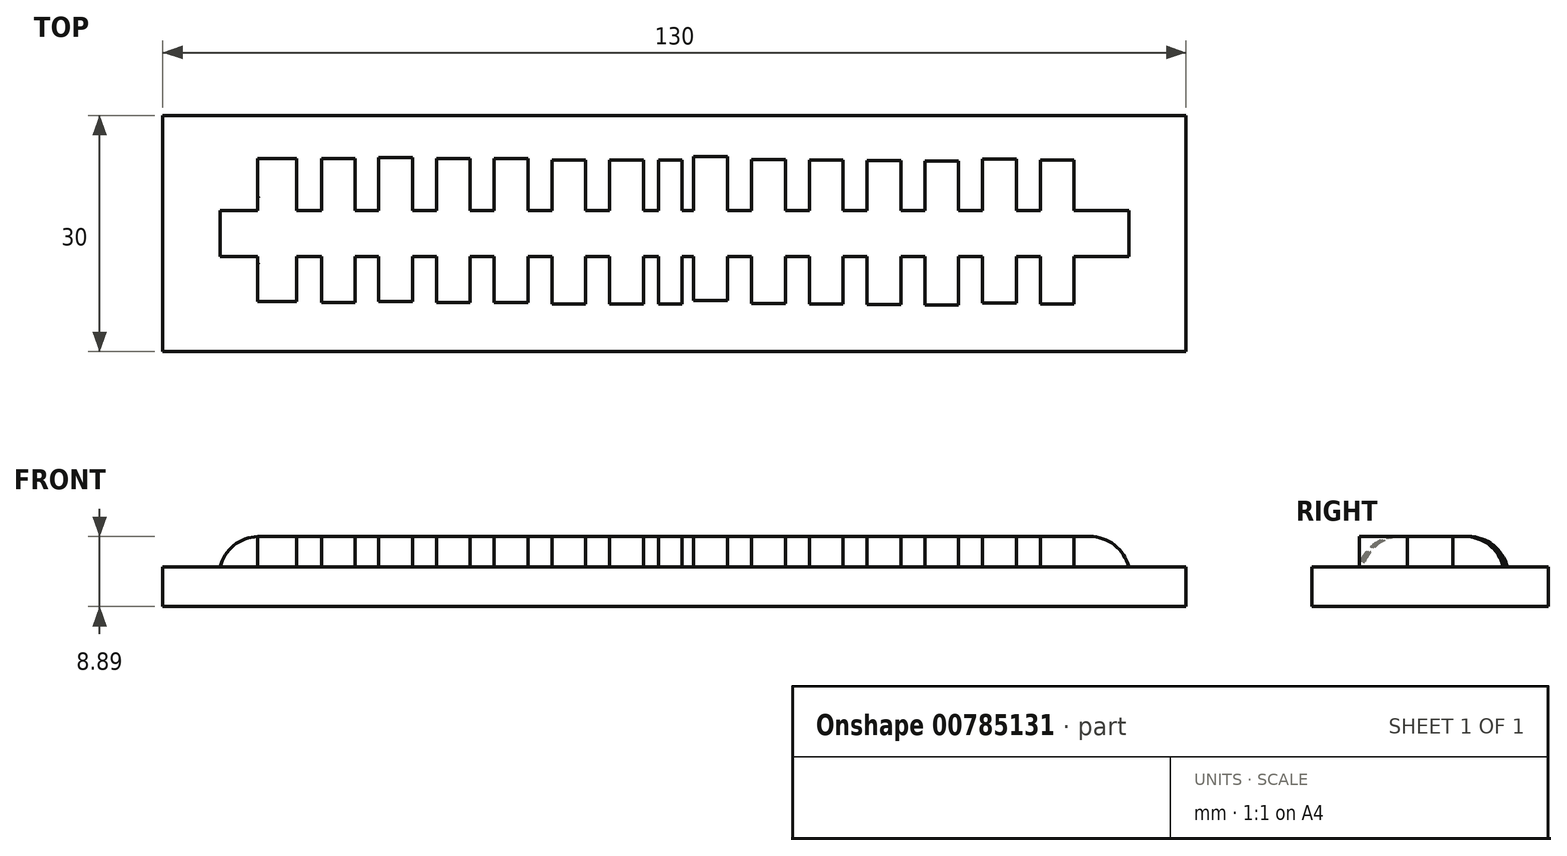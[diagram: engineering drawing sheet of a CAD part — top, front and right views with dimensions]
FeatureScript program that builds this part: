
annotation { "Feature Type Name" : "Feature", "Feature Type Description" : "" }
export const myFeature = defineFeature(function(context is Context, id is Id, definition is map)
    precondition{}
    {
        {
            var Q0;
            Q0=qCreatedBy(makeId("Top.planeOp"),FACE);
            var sketch = newSketch(context, id + "F0", { "sketchPlane" : qUnion([Q0])});
            skLineSegment(sketch, "E0.bottom", {"start": v(-65, 15) * mm, "end": v(65, 15) * mm});
            skLineSegment(sketch, "E0.top", {"start": v(-65, -15) * mm, "end": v(65, -15) * mm});
            skLineSegment(sketch, "E0.left", {"start": v(-65, 15) * mm, "end": v(-65, -15) * mm});
            skLineSegment(sketch, "E0.right", {"start": v(65, 15) * mm, "end": v(65, -15) * mm});
            skPoint(sketch, "E0.middle", {"position": v(0, 0) * mm});
            skSolve(sketch);
        }
        {
            var Q0;
            Q0 = qSketchRegion(id + "F0", true);
            extrude(context, id + "F1", {"entities" : qUnion([Q0]), "depth" : 5 * mm, "offsetDistance" : 25.4 * mm});
        }
        {
            var Q0;
            Q0=qCreatedBy(makeId("Top.planeOp"),FACE);
            var sketch = newSketch(context, id + "F2", { "sketchPlane" : qUnion([Q0])});
            skLineSegment(sketch, "E1.bottom", {"start": v(50.77, 9.32) * mm, "end": v(46.48, 9.32) * mm});
            skLineSegment(sketch, "E1.top", {"start": v(50.77, -8.97) * mm, "end": v(46.48, -8.97) * mm});
            skLineSegment(sketch, "E1.left", {"start": v(50.77, 9.32) * mm, "end": v(50.77, -8.97) * mm});
            skLineSegment(sketch, "E1.right", {"start": v(46.48, 9.32) * mm, "end": v(46.48, -8.97) * mm});
            skLineSegment(sketch, "E2.bottom", {"start": v(43.43, 9.43) * mm, "end": v(39.14, 9.43) * mm});
            skLineSegment(sketch, "E2.top", {"start": v(43.43, -8.85) * mm, "end": v(39.14, -8.85) * mm});
            skLineSegment(sketch, "E2.left", {"start": v(43.43, 9.43) * mm, "end": v(43.43, -8.85) * mm});
            skLineSegment(sketch, "E2.right", {"start": v(39.14, 9.43) * mm, "end": v(39.14, -8.85) * mm});
            skLineSegment(sketch, "E3", {"start": v(50.77, -8.97) * mm, "end": v(-46.32, -8.97) * mm});
            skLineSegment(sketch, "E4.bottom", {"start": v(36.1, 9.2) * mm, "end": v(31.8, 9.2) * mm});
            skLineSegment(sketch, "E4.top", {"start": v(36.1, -9.08) * mm, "end": v(31.8, -9.08) * mm});
            skLineSegment(sketch, "E4.left", {"start": v(36.1, 9.2) * mm, "end": v(36.1, -9.08) * mm});
            skLineSegment(sketch, "E4.right", {"start": v(31.8, 9.2) * mm, "end": v(31.8, -9.08) * mm});
            skLineSegment(sketch, "E5.bottom", {"start": v(28.75, 9.25) * mm, "end": v(24.46, 9.25) * mm});
            skLineSegment(sketch, "E5.top", {"start": v(28.75, -9.04) * mm, "end": v(24.46, -9.04) * mm});
            skLineSegment(sketch, "E5.left", {"start": v(28.75, 9.25) * mm, "end": v(28.75, -9.04) * mm});
            skLineSegment(sketch, "E5.right", {"start": v(24.46, 9.25) * mm, "end": v(24.46, -9.04) * mm});
            skLineSegment(sketch, "E6.bottom", {"start": v(21.42, 9.3) * mm, "end": v(17.13, 9.3) * mm});
            skLineSegment(sketch, "E6.top", {"start": v(21.42, -8.99) * mm, "end": v(17.13, -8.99) * mm});
            skLineSegment(sketch, "E6.left", {"start": v(21.42, 9.3) * mm, "end": v(21.42, -8.99) * mm});
            skLineSegment(sketch, "E6.right", {"start": v(17.13, 9.3) * mm, "end": v(17.13, -8.99) * mm});
            skLineSegment(sketch, "E7.bottom", {"start": v(14.08, 9.39) * mm, "end": v(9.79, 9.39) * mm});
            skLineSegment(sketch, "E7.top", {"start": v(14.08, -8.9) * mm, "end": v(9.79, -8.9) * mm});
            skLineSegment(sketch, "E7.left", {"start": v(14.08, 9.39) * mm, "end": v(14.08, -8.9) * mm});
            skLineSegment(sketch, "E7.right", {"start": v(9.79, 9.39) * mm, "end": v(9.79, -8.9) * mm});
            skLineSegment(sketch, "E8.bottom", {"start": v(6.74, 9.8) * mm, "end": v(2.45, 9.8) * mm});
            skLineSegment(sketch, "E8.top", {"start": v(6.74, -8.5) * mm, "end": v(2.45, -8.5) * mm});
            skLineSegment(sketch, "E8.left", {"start": v(6.74, 9.8) * mm, "end": v(6.74, -8.5) * mm});
            skLineSegment(sketch, "E8.right", {"start": v(2.45, 9.8) * mm, "end": v(2.45, -8.5) * mm});
            skLineSegment(sketch, "E9.bottom", {"start": v(-3.92, 9.33) * mm, "end": v(-8.21, 9.33) * mm});
            skLineSegment(sketch, "E9.top", {"start": v(-3.92, -8.95) * mm, "end": v(-8.21, -8.95) * mm});
            skLineSegment(sketch, "E9.left", {"start": v(-3.92, 9.33) * mm, "end": v(-3.92, -8.95) * mm});
            skLineSegment(sketch, "E9.right", {"start": v(-8.21, 9.33) * mm, "end": v(-8.21, -8.95) * mm});
            skLineSegment(sketch, "E10.bottom", {"start": v(-11.26, 9.33) * mm, "end": v(-15.55, 9.33) * mm});
            skLineSegment(sketch, "E10.top", {"start": v(-11.26, -8.95) * mm, "end": v(-15.55, -8.95) * mm});
            skLineSegment(sketch, "E10.left", {"start": v(-11.26, 9.33) * mm, "end": v(-11.26, -8.95) * mm});
            skLineSegment(sketch, "E10.right", {"start": v(-15.55, 9.33) * mm, "end": v(-15.55, -8.95) * mm});
            skLineSegment(sketch, "E11.bottom", {"start": v(-18.6, 9.49) * mm, "end": v(-22.89, 9.49) * mm});
            skLineSegment(sketch, "E11.top", {"start": v(-18.6, -8.8) * mm, "end": v(-22.89, -8.8) * mm});
            skLineSegment(sketch, "E11.left", {"start": v(-18.6, 9.49) * mm, "end": v(-18.6, -8.8) * mm});
            skLineSegment(sketch, "E11.right", {"start": v(-22.89, 9.49) * mm, "end": v(-22.89, -8.8) * mm});
            skLineSegment(sketch, "E12.bottom", {"start": v(-25.94, 9.5) * mm, "end": v(-30.23, 9.5) * mm});
            skLineSegment(sketch, "E12.top", {"start": v(-25.94, -8.78) * mm, "end": v(-30.23, -8.78) * mm});
            skLineSegment(sketch, "E12.left", {"start": v(-25.94, 9.5) * mm, "end": v(-25.94, -8.78) * mm});
            skLineSegment(sketch, "E12.right", {"start": v(-30.23, 9.5) * mm, "end": v(-30.23, -8.78) * mm});
            skLineSegment(sketch, "E13.bottom", {"start": v(-33.27, 9.65) * mm, "end": v(-37.56, 9.65) * mm});
            skLineSegment(sketch, "E13.top", {"start": v(-33.27, -8.64) * mm, "end": v(-37.56, -8.64) * mm});
            skLineSegment(sketch, "E13.left", {"start": v(-33.27, 9.65) * mm, "end": v(-33.27, -8.64) * mm});
            skLineSegment(sketch, "E13.right", {"start": v(-37.56, 9.65) * mm, "end": v(-37.56, -8.64) * mm});
            skLineSegment(sketch, "E14.bottom", {"start": v(-40.54, 9.49) * mm, "end": v(-44.83, 9.49) * mm});
            skLineSegment(sketch, "E14.top", {"start": v(-40.54, -8.8) * mm, "end": v(-44.83, -8.8) * mm});
            skLineSegment(sketch, "E14.left", {"start": v(-40.54, 9.49) * mm, "end": v(-40.54, -8.8) * mm});
            skLineSegment(sketch, "E14.right", {"start": v(-44.83, 9.49) * mm, "end": v(-44.83, -8.8) * mm});
            skLineSegment(sketch, "E15.bottom", {"start": v(0, 11.59) * mm, "end": v(0, 11.59) * mm});
            skLineSegment(sketch, "E15.top", {"start": v(0, -11.59) * mm, "end": v(0, -11.59) * mm});
            skPoint(sketch, "E15.middle", {"position": v(0, 0) * mm});
            skLineSegment(sketch, "E16.bottom", {"start": v(-2.01, 9.33) * mm, "end": v(0.98, 9.33) * mm});
            skLineSegment(sketch, "E16.top", {"start": v(-2.01, -8.97) * mm, "end": v(0.98, -8.97) * mm});
            skLineSegment(sketch, "E16.left", {"start": v(-2.01, 9.33) * mm, "end": v(-2.01, -8.97) * mm});
            skLineSegment(sketch, "E16.right", {"start": v(0.98, 9.33) * mm, "end": v(0.98, -8.97) * mm});
            skLineSegment(sketch, "E17.bottom", {"start": v(-52.93, 9.49) * mm, "end": v(-48, 9.49) * mm});
            skLineSegment(sketch, "E17.top", {"start": v(-52.93, -8.64) * mm, "end": v(-48, -8.64) * mm});
            skLineSegment(sketch, "E17.left", {"start": v(-52.93, 9.49) * mm, "end": v(-52.93, -8.64) * mm});
            skLineSegment(sketch, "E17.right", {"start": v(-48, 9.49) * mm, "end": v(-48, -8.64) * mm});
            skSolve(sketch);
        }
        {
            var Q0;
            Q0 = qSketchRegion(id + "F2", true);
            extrude(context, id + "F3", {"entities" : qUnion([Q0]), "operationType" : NewBodyOperationType.ADD, "depth" : 8.9 * mm, "offsetDistance" : 25.4 * mm});
        }
        {
            var Q0;
            Q0=qCreatedBy(makeId("Top.planeOp"),FACE);
            var sketch = newSketch(context, id + "F4", { "sketchPlane" : qUnion([Q0])});
            skLineSegment(sketch, "E18.bottom", {"start": v(-57.7, 2.9) * mm, "end": v(57.7, 2.9) * mm});
            skLineSegment(sketch, "E18.top", {"start": v(-57.7, -2.9) * mm, "end": v(57.7, -2.9) * mm});
            skLineSegment(sketch, "E18.left", {"start": v(-57.7, 2.9) * mm, "end": v(-57.7, -2.9) * mm});
            skLineSegment(sketch, "E18.right", {"start": v(57.7, 2.9) * mm, "end": v(57.7, -2.9) * mm});
            skPoint(sketch, "E18.middle", {"position": v(0, 0) * mm});
            skPoint(sketch, "E19", {"position": v(52.88, 2.9) * mm});
            skPoint(sketch, "E20", {"position": v(-52.88, 2.9) * mm});
            skSolve(sketch);
        }
        {
            var Q0;
            Q0 = qSketchRegion(id + "F4", true);
            extrude(context, id + "F5", {"entities" : qUnion([Q0]), "operationType" : NewBodyOperationType.ADD, "depth" : 8.9 * mm, "offsetDistance" : 25.4 * mm});
        }
        {
            var Q0;
            Q0=makeQuery(id+"F3.opExtrude","CAP_EDGE",EDGE,{"disambiguationData":[OSD([sQuery(id+"F2.wireOp",EDGE,"E3")])],"isStart":false});
            var Q1;
            Q1=makeQuery(id+"F3.opExtrude","CAP_EDGE",EDGE,{"disambiguationData":[OSD([sQuery(id+"F2.wireOp",EDGE,"E1.bottom")])],"isStart":false});
            var Q2;
            Q2=makeQuery(id+"F3.opExtrude","CAP_EDGE",EDGE,{"disambiguationData":[OSD([sQuery(id+"F2.wireOp",EDGE,"E2.bottom")])],"isStart":false});
            var Q3;
            Q3=makeQuery(id+"F3.opExtrude","CAP_EDGE",EDGE,{"disambiguationData":[OSD([sQuery(id+"F2.wireOp",EDGE,"E2.top")])],"isStart":false});
            var Q4;
            Q4=makeQuery(id+"F3.opExtrude","CAP_EDGE",EDGE,{"disambiguationData":[OSD([sQuery(id+"F2.wireOp",EDGE,"E4.top")])],"isStart":false});
            var Q5;
            Q5=makeQuery(id+"F3.opExtrude","CAP_EDGE",EDGE,{"disambiguationData":[OSD([sQuery(id+"F2.wireOp",EDGE,"E4.bottom")])],"isStart":false});
            var Q6;
            Q6=makeQuery(id+"F3.opExtrude","CAP_EDGE",EDGE,{"disambiguationData":[OSD([sQuery(id+"F2.wireOp",EDGE,"E5.top")])],"isStart":false});
            var Q7;
            Q7=makeQuery(id+"F3.opExtrude","CAP_EDGE",EDGE,{"disambiguationData":[OSD([sQuery(id+"F2.wireOp",EDGE,"E5.bottom")])],"isStart":false});
            var Q8;
            Q8=makeQuery(id+"F3.opExtrude","CAP_EDGE",EDGE,{"disambiguationData":[OSD([sQuery(id+"F2.wireOp",EDGE,"E6.bottom")])],"isStart":false});
            var Q9;
            Q9=makeQuery(id+"F3.opExtrude","CAP_EDGE",EDGE,{"disambiguationData":[OSD([sQuery(id+"F2.wireOp",EDGE,"E6.top")])],"isStart":false});
            var Q10;
            Q10=makeQuery(id+"F3.opExtrude","CAP_EDGE",EDGE,{"disambiguationData":[OSD([sQuery(id+"F2.wireOp",EDGE,"E7.top")])],"isStart":false});
            var Q11;
            Q11=makeQuery(id+"F3.opExtrude","CAP_EDGE",EDGE,{"disambiguationData":[OSD([sQuery(id+"F2.wireOp",EDGE,"E7.bottom")])],"isStart":false});
            var Q12;
            Q12=makeQuery(id+"F3.opExtrude","CAP_EDGE",EDGE,{"disambiguationData":[OSD([sQuery(id+"F2.wireOp",EDGE,"E8.top")])],"isStart":false});
            var Q13;
            Q13=makeQuery(id+"F3.opExtrude","CAP_EDGE",EDGE,{"disambiguationData":[OSD([sQuery(id+"F2.wireOp",EDGE,"E8.bottom")])],"isStart":false});
            var Q14;
            Q14=makeQuery(id+"F3.opExtrude","CAP_EDGE",EDGE,{"disambiguationData":[OSD([sQuery(id+"F2.wireOp",EDGE,"E16.bottom")])],"isStart":false});
            var Q15;
            Q15=makeQuery(id+"F3.opExtrude","CAP_EDGE",EDGE,{"disambiguationData":[OSD([sQuery(id+"F2.wireOp",EDGE,"E9.bottom")])],"isStart":false});
            var Q16;
            Q16=makeQuery(id+"F3.opExtrude","CAP_EDGE",EDGE,{"disambiguationData":[OSD([sQuery(id+"F2.wireOp",EDGE,"E10.bottom")])],"isStart":false});
            var Q17;
            Q17=makeQuery(id+"F3.opExtrude","CAP_EDGE",EDGE,{"disambiguationData":[OSD([sQuery(id+"F2.wireOp",EDGE,"E11.bottom")])],"isStart":false});
            var Q18;
            Q18=makeQuery(id+"F3.opExtrude","CAP_EDGE",EDGE,{"disambiguationData":[OSD([sQuery(id+"F2.wireOp",EDGE,"E12.bottom")])],"isStart":false});
            var Q19;
            Q19=makeQuery(id+"F3.opExtrude","CAP_EDGE",EDGE,{"disambiguationData":[OSD([sQuery(id+"F2.wireOp",EDGE,"E13.bottom")])],"isStart":false});
            var Q20;
            Q20=makeQuery(id+"F3.opExtrude","CAP_EDGE",EDGE,{"disambiguationData":[OSD([sQuery(id+"F2.wireOp",EDGE,"E14.bottom")])],"isStart":false});
            var Q21;
            Q21=makeQuery(id+"F3.opExtrude","CAP_EDGE",EDGE,{"disambiguationData":[OSD([sQuery(id+"F2.wireOp",EDGE,"E14.top")])],"isStart":false});
            var Q22;
            Q22=makeQuery(id+"F3.opExtrude","CAP_EDGE",EDGE,{"disambiguationData":[OSD([sQuery(id+"F2.wireOp",EDGE,"E13.top")])],"isStart":false});
            var Q23;
            Q23=makeQuery(id+"F3.opExtrude","CAP_EDGE",EDGE,{"disambiguationData":[OSD([sQuery(id+"F2.wireOp",EDGE,"E12.top")])],"isStart":false});
            var Q24;
            Q24=makeQuery(id+"F3.opExtrude","CAP_EDGE",EDGE,{"disambiguationData":[OSD([sQuery(id+"F2.wireOp",EDGE,"E11.top")])],"isStart":false});
            var Q25;
            Q25=makeQuery(id+"F3.opExtrude","CAP_EDGE",EDGE,{"disambiguationData":[OSD([sQuery(id+"F2.wireOp",EDGE,"E10.top")])],"isStart":false});
            var Q26;
            Q26=makeQuery(id+"F3.opExtrude","CAP_EDGE",EDGE,{"disambiguationData":[OSD([sQuery(id+"F2.wireOp",EDGE,"E9.top")])],"isStart":false});
            var Q27;
            Q27=makeQuery(id+"F5.opExtrude","CAP_EDGE",EDGE,{"disambiguationData":[OSD([sQuery(id+"F4.wireOp",EDGE,"E18.left")])],"isStart":false});
            var Q28;
            Q28=makeQuery(id+"F5.opExtrude","CAP_EDGE",EDGE,{"disambiguationData":[OSD([sQuery(id+"F4.wireOp",EDGE,"E18.right")])],"isStart":false});
            var Q29;
            Q29=makeQuery(id+"F3.opExtrude","CAP_EDGE",EDGE,{"disambiguationData":[OSD([sQuery(id+"F2.wireOp",EDGE,"E16.top")])],"isStart":false});
            var Q30;
            Q30=makeQuery(id+"F3.opExtrude","CAP_EDGE",EDGE,{"disambiguationData":[OSD([sQuery(id+"F2.wireOp",EDGE,"E17.top")])],"isStart":false});
            var Q31;
            Q31=makeQuery(id+"F3.opExtrude","CAP_EDGE",EDGE,{"disambiguationData":[OSD([sQuery(id+"F2.wireOp",EDGE,"E17.bottom")])],"isStart":false});
            fillet(context, id + "F6", {"entities" : qUnion([Q0, Q1, Q2, Q3, Q4, Q5, Q6, Q7, Q8, Q9, Q10, Q11, Q12, Q13, Q14, Q15, Q16, Q17, Q18, Q19, Q20, Q21, Q22, Q23, Q24, Q25, Q26, Q27, Q28, Q29, Q30, Q31]), "radius" : 5.08 * mm, "tangentPropagation" : true, "allowEdgeOverflow" : false});
        }
    });
